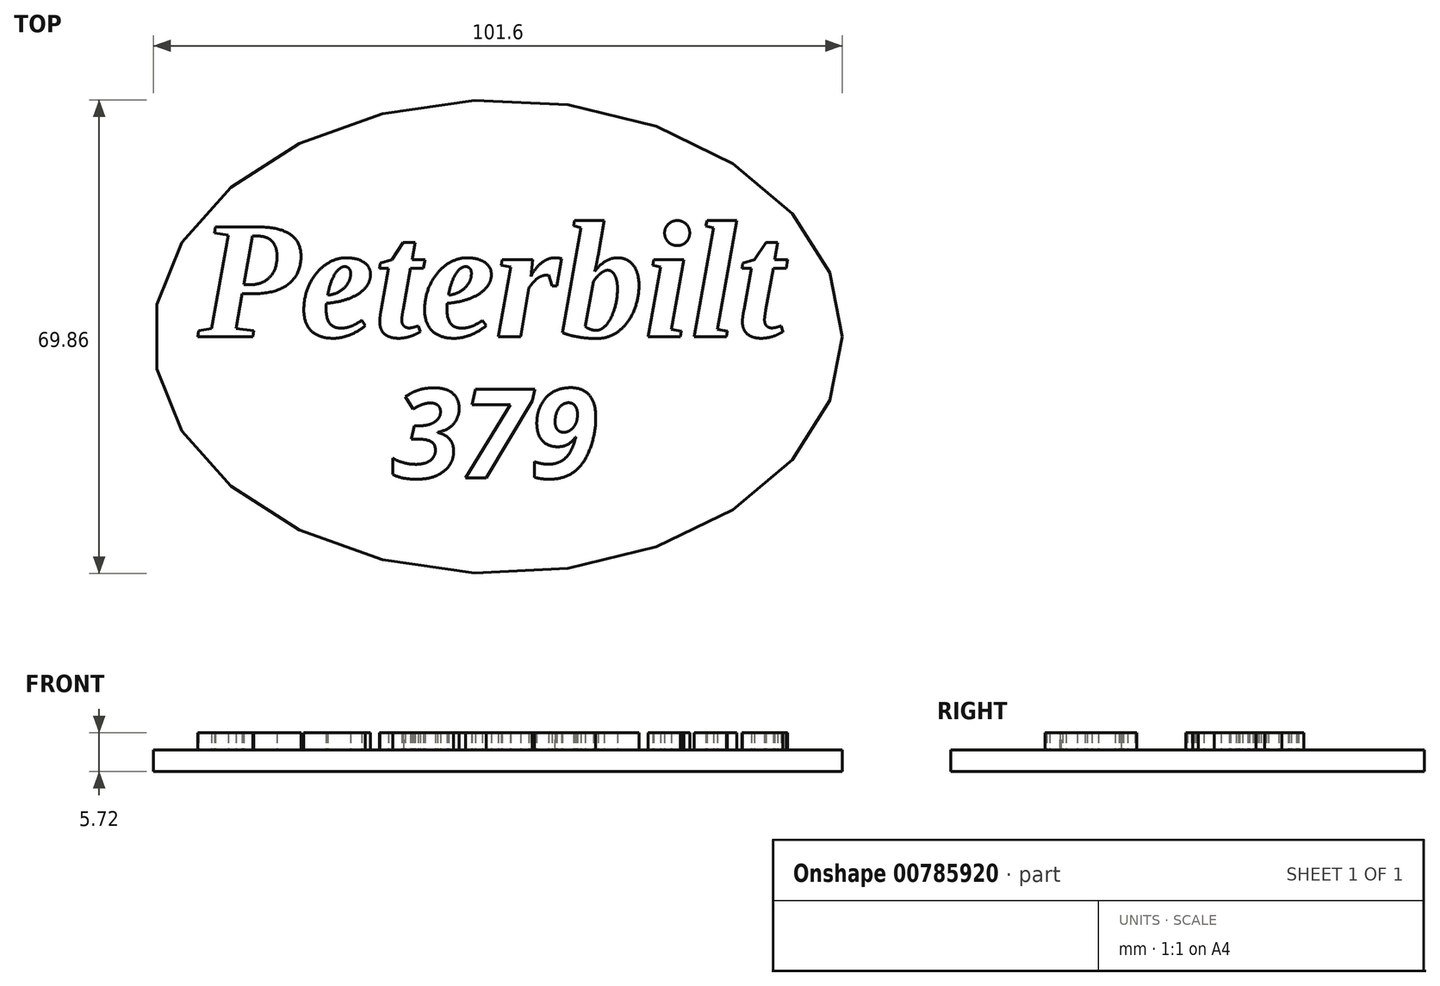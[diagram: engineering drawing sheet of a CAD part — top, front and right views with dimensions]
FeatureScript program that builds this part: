
annotation { "Feature Type Name" : "Feature", "Feature Type Description" : "" }
export const myFeature = defineFeature(function(context is Context, id is Id, definition is map)
    precondition{}
    {
        {
            var Q0;
            Q0=qCreatedBy(makeId("Top.planeOp"),FACE);
            var sketch = newSketch(context, id + "F0", { "sketchPlane" : qUnion([Q0])});
            skEllipse(sketch, "E0", {"center": v(0, 0) * mm, "majorRadius": 50.8 * mm, "minorRadius": 34.93 * mm, "majorAxis": v(1, 0)});
            skPoint(sketch, "E1", {"position": v(0, 34.93) * mm});
            skSolve(sketch);
        }
        {
            var Q0;
            Q0=makeQuery(id+"F0.imprint","IMPRINT",FACE,{"disambiguationData":[TD([[makeQuery(id+"F0.imprint","IMPRINT",EDGE,{"derivedFrom":sQuery(id+"F0.wireOp",EDGE,"E0")}),1.0]])]});
            extrude(context, id + "F1", {"entities" : qUnion([Q0]), "depth" : 3.17 * mm, "offsetDistance" : 25.4 * mm});
        }
        {
            var Q0;
            Q0=makeQuery(id+"F1.opExtrude","CAP_FACE",FACE,{"disambiguationData":[OSD([sQuery(id+"F0.wireOp",EDGE,"E0")])],"isStart":false});
            var sketch = newSketch(context, id + "F2", { "sketchPlane" : qUnion([Q0])});
            skText(sketch, "E2", { "text": "Peterbilt", "fontName": "Tinos-BoldItalic.ttf"});
            skText(sketch, "E3", { "text": "379", "fontName": "OpenSans-BoldItalic.ttf"});
            const initialGuessF2  = {"E2": [-0.04429, 0, 1, 0, 0.01778], "E3": [-0.01563, -0.02086, 1, 0, 0.01324]};
            skSetInitialGuess(sketch, initialGuessF2);
            skSolve(sketch);
        }
        {
            var Q0;
            Q0 = qSketchRegion(id + "F2", true);
            extrude(context, id + "F3", {"entities" : qUnion([Q0]), "operationType" : NewBodyOperationType.ADD, "depth" : 2.54 * mm, "offsetDistance" : 25.4 * mm});
        }
    });
